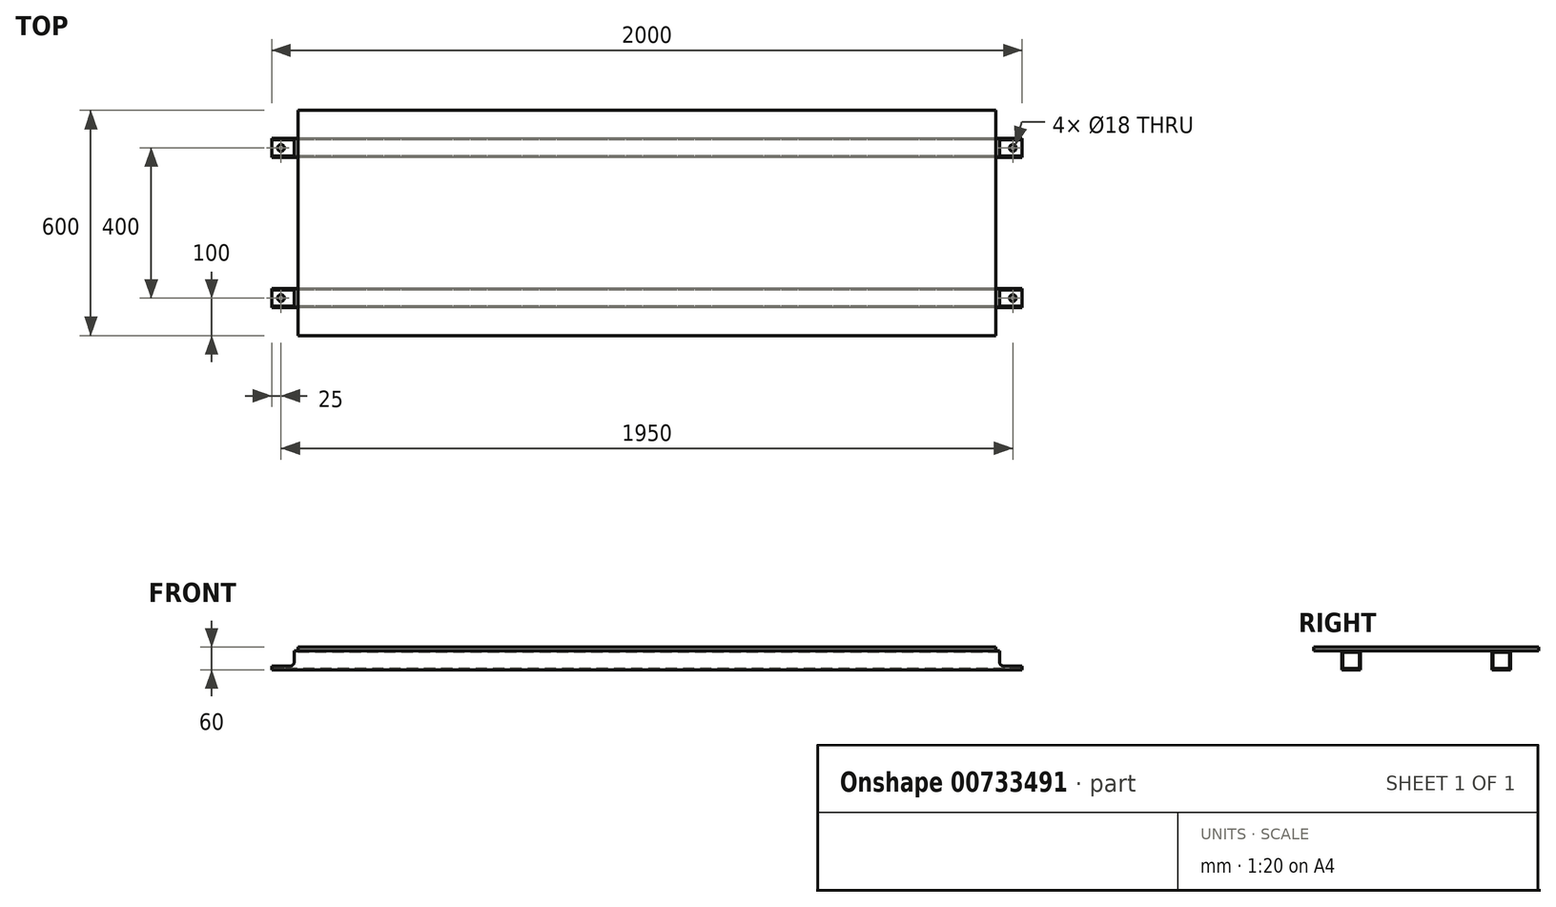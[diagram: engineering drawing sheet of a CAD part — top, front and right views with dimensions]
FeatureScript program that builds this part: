
annotation { "Feature Type Name" : "Feature", "Feature Type Description" : "" }
export const myFeature = defineFeature(function(context is Context, id is Id, definition is map)
    precondition{}
    {
        {
            var Q0;
            Q0=qCreatedBy(makeId("Right.planeOp"),FACE);
            var sketch = newSketch(context, id + "F0", { "sketchPlane" : qUnion([Q0])});
            skLineSegment(sketch, "E0.bottom", {"start": v(-225, -25) * mm, "end": v(-175, -25) * mm});
            skLineSegment(sketch, "E0.top", {"start": v(-225, 25) * mm, "end": v(-175, 25) * mm});
            skLineSegment(sketch, "E0.left", {"start": v(-225, -25) * mm, "end": v(-225, 25) * mm});
            skLineSegment(sketch, "E0.right", {"start": v(-175, -25) * mm, "end": v(-175, 25) * mm});
            skLineSegment(sketch, "E1.bottom", {"start": v(-222, 22) * mm, "end": v(-178, 22) * mm});
            skLineSegment(sketch, "E1.top", {"start": v(-222, -22) * mm, "end": v(-178, -22) * mm});
            skLineSegment(sketch, "E1.left", {"start": v(-222, 22) * mm, "end": v(-222, -22) * mm});
            skLineSegment(sketch, "E1.right", {"start": v(-178, 22) * mm, "end": v(-178, -22) * mm});
            skLineSegment(sketch, "E2.MirrorCS", {"start": v(225, -25) * mm, "end": v(175, -25) * mm});
            skLineSegment(sketch, "E3.MirrorCS", {"start": v(225, 25) * mm, "end": v(175, 25) * mm});
            skLineSegment(sketch, "E4.MirrorCS", {"start": v(222, 22) * mm, "end": v(222, -22) * mm});
            skLineSegment(sketch, "E5.MirrorCS", {"start": v(225, -25) * mm, "end": v(225, 25) * mm});
            skLineSegment(sketch, "E6.MirrorCS", {"start": v(222, -22) * mm, "end": v(178, -22) * mm});
            skLineSegment(sketch, "E7.MirrorCS", {"start": v(222, 22) * mm, "end": v(178, 22) * mm});
            skLineSegment(sketch, "E8.MirrorCS", {"start": v(175, -25) * mm, "end": v(175, 25) * mm});
            skLineSegment(sketch, "E9.MirrorCS", {"start": v(178, 22) * mm, "end": v(178, -22) * mm});
            skSolve(sketch);
        }
        {
            var Q0;
            Q0 = qSketchRegion(id + "F0", true);
            extrude(context, id + "F1", {"entities" : qUnion([Q0]), "endBound" : BoundingType.SYMMETRIC, "depth" : 2000 * mm, "offsetDistance" : 25 * mm});
        }
        {
            var Q0;
            Q0=makeQuery(id+"F1.opExtrude","SWEPT_FACE",FACE,{"disambiguationData":[OSD([sQuery(id+"F0.wireOp",EDGE,"E0.top")])]});
            var sketch = newSketch(context, id + "F2", { "sketchPlane" : qUnion([Q0])});
            skLineSegment(sketch, "E10.bottom", {"start": v(-930, -300) * mm, "end": v(930, -300) * mm});
            skLineSegment(sketch, "E10.top", {"start": v(-930, 300) * mm, "end": v(930, 300) * mm});
            skLineSegment(sketch, "E10.left", {"start": v(-930, -300) * mm, "end": v(-930, 300) * mm});
            skLineSegment(sketch, "E10.right", {"start": v(930, -300) * mm, "end": v(930, 300) * mm});
            skSolve(sketch);
        }
        {
            var Q0;
            Q0 = qSketchRegion(id + "F2", true);
            extrude(context, id + "F3", {"entities" : qUnion([Q0]), "depth" : 10 * mm, "offsetDistance" : 25 * mm});
        }
        {
            var Q0;
            Q0=makeQuery(id+"F1.opExtrude","SWEPT_FACE",FACE,{"disambiguationData":[OSD([sQuery(id+"F0.wireOp",EDGE,"E3.MirrorCS")])]});
            var sketch = newSketch(context, id + "F4", { "sketchPlane" : qUnion([Q0])});
            skLineSegment(sketch, "E11.bottom", {"start": v(-1000, 175) * mm, "end": v(-940, 175) * mm});
            skLineSegment(sketch, "E11.top", {"start": v(-1000, 225) * mm, "end": v(-940, 225) * mm});
            skLineSegment(sketch, "E11.left", {"start": v(-1000, 175) * mm, "end": v(-1000, 225) * mm});
            skLineSegment(sketch, "E11.right", {"start": v(-940, 175) * mm, "end": v(-940, 225) * mm});
            skLineSegment(sketch, "E12.MirrorCS", {"start": v(-1000, -175) * mm, "end": v(-1000, -225) * mm});
            skLineSegment(sketch, "E13.MirrorCS", {"start": v(-1000, -225) * mm, "end": v(-940, -225) * mm});
            skLineSegment(sketch, "E14.MirrorCS", {"start": v(-1000, -175) * mm, "end": v(-940, -175) * mm});
            skLineSegment(sketch, "E15.MirrorCS", {"start": v(-940, -175) * mm, "end": v(-940, -225) * mm});
            skLineSegment(sketch, "E16.MirrorCS", {"start": v(1000, 175) * mm, "end": v(940, 175) * mm});
            skLineSegment(sketch, "E17.MirrorCS", {"start": v(1000, 225) * mm, "end": v(940, 225) * mm});
            skLineSegment(sketch, "E18.MirrorCS", {"start": v(1000, 175) * mm, "end": v(1000, 225) * mm});
            skLineSegment(sketch, "E19.MirrorCS", {"start": v(1000, -225) * mm, "end": v(940, -225) * mm});
            skLineSegment(sketch, "E20.MirrorCS", {"start": v(940, 175) * mm, "end": v(940, 225) * mm});
            skLineSegment(sketch, "E21.MirrorCS", {"start": v(1000, -175) * mm, "end": v(940, -175) * mm});
            skLineSegment(sketch, "E22.MirrorCS", {"start": v(1000, -175) * mm, "end": v(1000, -225) * mm});
            skLineSegment(sketch, "E23.MirrorCS", {"start": v(940, -175) * mm, "end": v(940, -225) * mm});
            skSolve(sketch);
        }
        {
            var Q0;
            Q0 = qSketchRegion(id + "F4", true);
            extrude(context, id + "F5", {"entities" : qUnion([Q0]), "operationType" : NewBodyOperationType.REMOVE, "oppositeDirection" : true, "depth" : 40 * mm, "offsetDistance" : 25 * mm});
        }
        {
            var Q0;
            {var subQ0=sQuery(id+"F4.wireOp",EDGE,"E11.right");Q0=makeQuery(id+"F5.boolean.opBoolean","COPY",EDGE,{"disambiguationData":[TD([makeQuery(id+"F1.opExtrude","SWEPT_FACE",FACE,{"disambiguationData":[OSD([sQuery(id+"F0.wireOp",EDGE,"E4.MirrorCS")])]})])],"derivedFrom":makeQuery(id+"F5.opExtrude","CAP_EDGE",EDGE,{"disambiguationData":[OSD([subQ0])],"isStart":false})});}
            var Q1;
            {var subQ0=sQuery(id+"F4.wireOp",EDGE,"E11.right");Q1=makeQuery(id+"F5.boolean.opBoolean","COPY",EDGE,{"disambiguationData":[TD([makeQuery(id+"F1.opExtrude","SWEPT_FACE",FACE,{"disambiguationData":[OSD([sQuery(id+"F0.wireOp",EDGE,"E8.MirrorCS")])]})])],"derivedFrom":makeQuery(id+"F5.opExtrude","CAP_EDGE",EDGE,{"disambiguationData":[OSD([subQ0])],"isStart":false})});}
            var Q2;
            {var subQ0=sQuery(id+"F4.wireOp",EDGE,"E15.MirrorCS");Q2=makeQuery(id+"F5.boolean.opBoolean","COPY",EDGE,{"disambiguationData":[TD([makeQuery(id+"F1.opExtrude","SWEPT_FACE",FACE,{"disambiguationData":[OSD([sQuery(id+"F0.wireOp",EDGE,"E0.right")])]})])],"derivedFrom":makeQuery(id+"F5.opExtrude","CAP_EDGE",EDGE,{"disambiguationData":[OSD([subQ0])],"isStart":false})});}
            var Q3;
            {var subQ0=sQuery(id+"F4.wireOp",EDGE,"E15.MirrorCS");Q3=makeQuery(id+"F5.boolean.opBoolean","COPY",EDGE,{"disambiguationData":[TD([makeQuery(id+"F1.opExtrude","SWEPT_FACE",FACE,{"disambiguationData":[OSD([sQuery(id+"F0.wireOp",EDGE,"E0.left")])]})])],"derivedFrom":makeQuery(id+"F5.opExtrude","CAP_EDGE",EDGE,{"disambiguationData":[OSD([subQ0])],"isStart":false})});}
            fillet(context, id + "F6", {"entities" : qUnion([Q0, Q1, Q2, Q3]), "radius" : 10 * mm, "tangentPropagation" : true, "allowEdgeOverflow" : false});
        }
        {
            var Q0;
            {var subQ0=sQuery(id+"F4.wireOp",EDGE,"E23.MirrorCS");Q0=makeQuery(id+"F5.boolean.opBoolean","COPY",EDGE,{"disambiguationData":[TD([makeQuery(id+"F1.opExtrude","SWEPT_FACE",FACE,{"disambiguationData":[OSD([sQuery(id+"F0.wireOp",EDGE,"E0.left")])]})])],"derivedFrom":makeQuery(id+"F5.opExtrude","CAP_EDGE",EDGE,{"disambiguationData":[OSD([subQ0])],"isStart":false})});}
            var Q1;
            {var subQ0=sQuery(id+"F4.wireOp",EDGE,"E23.MirrorCS");Q1=makeQuery(id+"F5.boolean.opBoolean","COPY",EDGE,{"disambiguationData":[TD([makeQuery(id+"F1.opExtrude","SWEPT_FACE",FACE,{"disambiguationData":[OSD([sQuery(id+"F0.wireOp",EDGE,"E0.right")])]})])],"derivedFrom":makeQuery(id+"F5.opExtrude","CAP_EDGE",EDGE,{"disambiguationData":[OSD([subQ0])],"isStart":false})});}
            var Q2;
            {var subQ0=sQuery(id+"F4.wireOp",EDGE,"E20.MirrorCS");Q2=makeQuery(id+"F5.boolean.opBoolean","COPY",EDGE,{"disambiguationData":[TD([makeQuery(id+"F1.opExtrude","SWEPT_FACE",FACE,{"disambiguationData":[OSD([sQuery(id+"F0.wireOp",EDGE,"E8.MirrorCS")])]})])],"derivedFrom":makeQuery(id+"F5.opExtrude","CAP_EDGE",EDGE,{"disambiguationData":[OSD([subQ0])],"isStart":false})});}
            var Q3;
            {var subQ0=sQuery(id+"F4.wireOp",EDGE,"E20.MirrorCS");Q3=makeQuery(id+"F5.boolean.opBoolean","COPY",EDGE,{"disambiguationData":[TD([makeQuery(id+"F1.opExtrude","SWEPT_FACE",FACE,{"disambiguationData":[OSD([sQuery(id+"F0.wireOp",EDGE,"E4.MirrorCS")])]})])],"derivedFrom":makeQuery(id+"F5.opExtrude","CAP_EDGE",EDGE,{"disambiguationData":[OSD([subQ0])],"isStart":false})});}
            fillet(context, id + "F7", {"entities" : qUnion([Q0, Q1, Q2, Q3]), "radius" : 10 * mm, "tangentPropagation" : true, "allowEdgeOverflow" : false});
        }
        {
            var Q0;
            Q0=makeQuery(id+"F1.opExtrude","SWEPT_FACE",FACE,{"disambiguationData":[OSD([sQuery(id+"F0.wireOp",EDGE,"E6.MirrorCS")])]});
            var sketch = newSketch(context, id + "F8", { "sketchPlane" : qUnion([Q0])});
            skCircle(sketch, "E24", {"center": v(-975, 200) * mm, "radius": 9 * mm});
            skCircle(sketch, "E25.0.1.0", {"center": v(-975, -200) * mm, "radius": 9 * mm});
            skCircle(sketch, "E25.1.0.0", {"center": v(975, 200) * mm, "radius": 9 * mm});
            skCircle(sketch, "E25.1.1.0", {"center": v(975, -200) * mm, "radius": 9 * mm});
            skCircle(sketch, "E25.2.0.0", {"center": v(2925, 200) * mm, "radius": 9 * mm});
            skCircle(sketch, "E25.2.1.0", {"center": v(2925, -200) * mm, "radius": 9 * mm});
            skLineSegment(sketch, "E25.direction1", {"start": v(-975, 200) * mm, "end": v(975, 200) * mm, "construction": true});
            skLineSegment(sketch, "E25.direction2", {"start": v(-975, 200) * mm, "end": v(-975, -200) * mm, "construction": true});
            skSolve(sketch);
        }
        {
            var Q0;
            Q0 = qSketchRegion(id + "F8", true);
            extrude(context, id + "F9", {"entities" : qUnion([Q0]), "operationType" : NewBodyOperationType.REMOVE, "oppositeDirection" : true, "depth" : 5 * mm, "offsetDistance" : 25 * mm});
        }
    });
